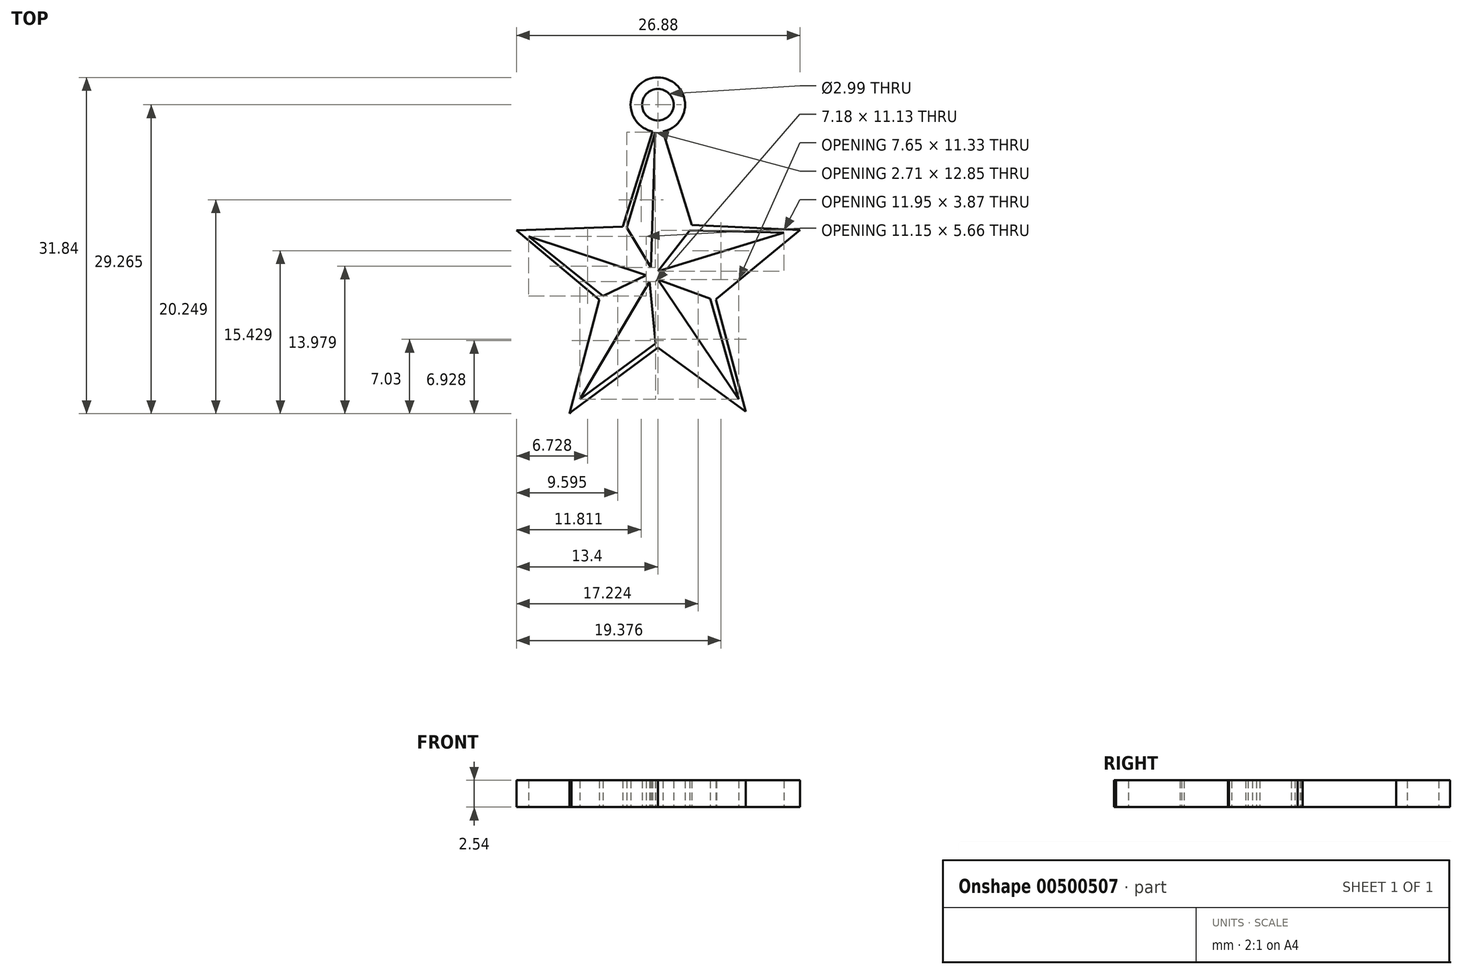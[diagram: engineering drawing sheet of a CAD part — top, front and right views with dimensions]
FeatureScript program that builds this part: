
annotation { "Feature Type Name" : "Feature", "Feature Type Description" : "" }
export const myFeature = defineFeature(function(context is Context, id is Id, definition is map)
    precondition{}
    {
        {
            var Q0;
            Q0=qCreatedBy(makeId("Top.planeOp"),FACE);
            var sketch = newSketch(context, id + "F0", { "sketchPlane" : qUnion([Q0])});
            skPoint(sketch, "E0.middle", {"position": v(0, 0) * mm});
            skPoint(sketch, "E1.startSnap0", {"position": v(-0.14, 12.9) * mm});
            skLineSegment(sketch, "E2", {"start": v(3.2, 2.5) * mm, "end": v(13.48, 2.02) * mm});
            skLineSegment(sketch, "E3", {"start": v(13.48, 2.02) * mm, "end": v(5.58, -4.5) * mm});
            skLineSegment(sketch, "E4", {"start": v(5.58, -4.5) * mm, "end": v(5.5, -4.6) * mm});
            skLineSegment(sketch, "E5", {"start": v(5.5, -4.6) * mm, "end": v(8.33, -15.2) * mm});
            skLineSegment(sketch, "E6", {"start": v(8.33, -15.2) * mm, "end": v(0, -9.13) * mm});
            skLineSegment(sketch, "E7", {"start": v(0, -9.13) * mm, "end": v(-8.2, -15.2) * mm});
            skLineSegment(sketch, "E8", {"start": v(-8.2, -15.2) * mm, "end": v(-8.38, -15.38) * mm});
            skLineSegment(sketch, "E9", {"start": v(-8.38, -15.38) * mm, "end": v(-5.53, -4.6) * mm});
            skLineSegment(sketch, "E10", {"start": v(-5.53, -4.6) * mm, "end": v(-13.4, 1.98) * mm});
            skLineSegment(sketch, "E11", {"start": v(-13.4, 1.98) * mm, "end": v(-3.34, 2.33) * mm});
            skLineSegment(sketch, "E12", {"start": v(-3.34, 2.33) * mm, "end": v(-0.49, 11.35) * mm});
            skLineSegment(sketch, "E13", {"start": v(-1.1, -2.26) * mm, "end": v(-5.19, -4.23) * mm});
            skLineSegment(sketch, "E14", {"start": v(-5.19, -4.23) * mm, "end": v(-12.25, 1.43) * mm});
            skLineSegment(sketch, "E15", {"start": v(-12.25, 1.43) * mm, "end": v(-1.1, -2.26) * mm});
            skLineSegment(sketch, "E16", {"start": v(0, -1.88) * mm, "end": v(3.04, 1.98) * mm});
            skLineSegment(sketch, "E17", {"start": v(3.04, 1.98) * mm, "end": v(11.95, 1.77) * mm});
            skLineSegment(sketch, "E18", {"start": v(11.95, 1.77) * mm, "end": v(0, -1.88) * mm});
            skLineSegment(sketch, "E19", {"start": v(-0.24, 11.3) * mm, "end": v(-0.65, -1.56) * mm});
            skLineSegment(sketch, "E20", {"start": v(-0.65, -1.56) * mm, "end": v(-2.94, 2.24) * mm});
            skLineSegment(sketch, "E21", {"start": v(-2.94, 2.24) * mm, "end": v(-0.24, 11.3) * mm});
            skLineSegment(sketch, "E22", {"start": v(7.65, -14.02) * mm, "end": v(0, -2.68) * mm});
            skLineSegment(sketch, "E23", {"start": v(0, -2.68) * mm, "end": v(4.95, -4.5) * mm});
            skLineSegment(sketch, "E24", {"start": v(4.95, -4.5) * mm, "end": v(7.65, -14.02) * mm});
            skLineSegment(sketch, "E25", {"start": v(-7.4, -14.02) * mm, "end": v(-0.79, -2.89) * mm});
            skLineSegment(sketch, "E26", {"start": v(-0.52, -8.97) * mm, "end": v(-7.4, -14.02) * mm});
            skLineSegment(sketch, "E27", {"start": v(-0.79, -2.89) * mm, "end": v(-0.21, -8.76) * mm});
            skLineSegment(sketch, "E28", {"start": v(-0.21, -8.76) * mm, "end": v(-0.52, -8.97) * mm});
            skArc(sketch, "E29", {"start": v(0.47, 11.35) * mm, "mid": v(0, 16.46) * mm, "end": v(-0.49, 11.35) * mm});
            skCircle(sketch, "E30", {"center": v(0, 13.89) * mm, "radius": 1.5 * mm});
            skLineSegment(sketch, "E31.trimOffspring", {"start": v(0.47, 11.35) * mm, "end": v(3.2, 2.5) * mm});
            skPoint(sketch, "E1.start.orphan", {"position": v(0, 12.9) * mm});
            skSolve(sketch);
        }
        {
            var Q0;
            Q0 = qSketchRegion(id + "F0", true);
            extrude(context, id + "F1", {"entities" : qUnion([Q0]), "depth" : 2.54 * mm});
        }
    });
